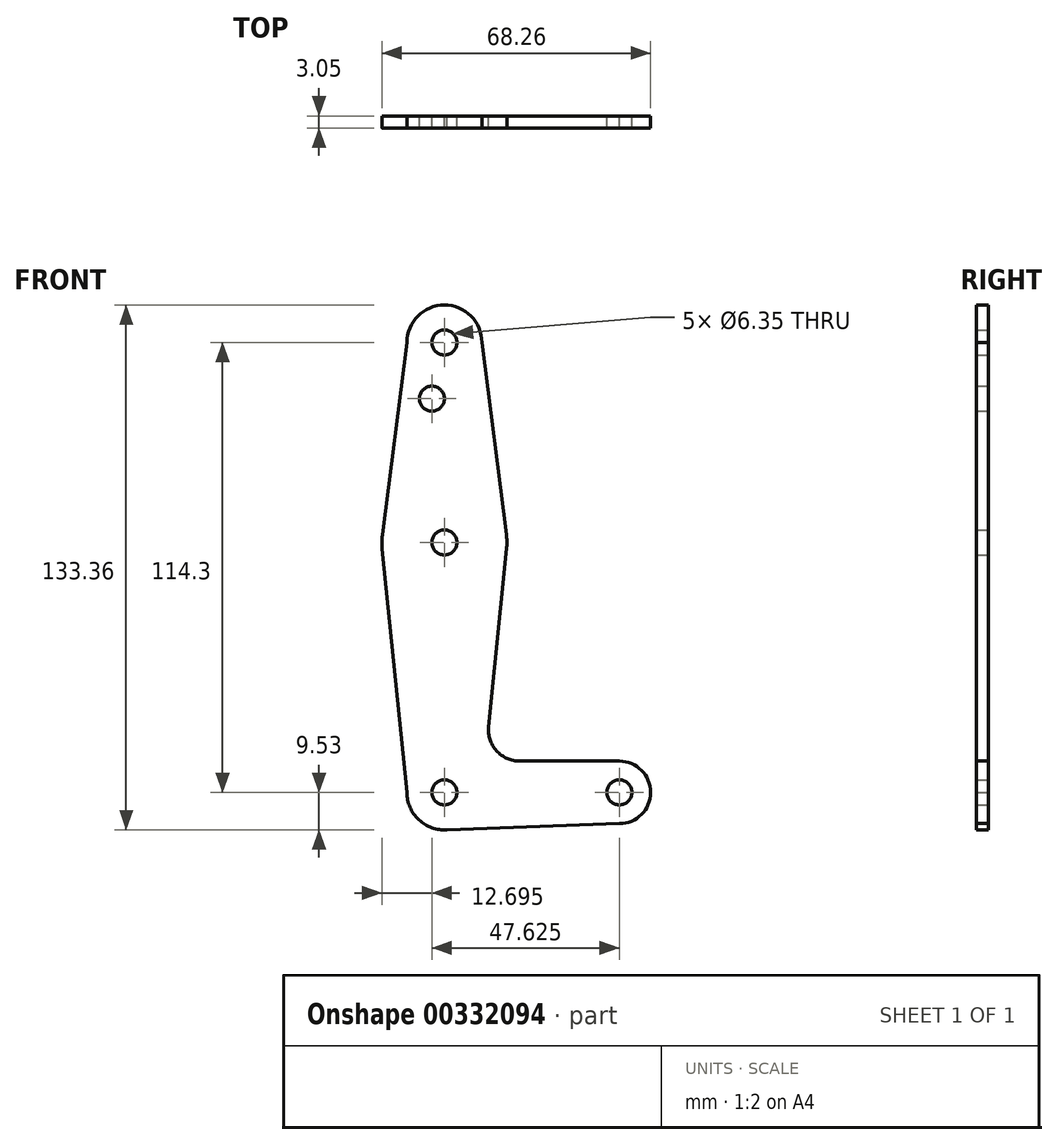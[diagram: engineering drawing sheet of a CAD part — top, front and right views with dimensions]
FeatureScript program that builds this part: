
annotation { "Feature Type Name" : "Feature", "Feature Type Description" : "" }
export const myFeature = defineFeature(function(context is Context, id is Id, definition is map)
    precondition{}
    {
        {
            var Q0;
            Q0=qCreatedBy(makeId("Front.planeOp"),FACE);
            var sketch = newSketch(context, id + "F0", { "sketchPlane" : qUnion([Q0])});
            skLineSegment(sketch, "E0", {"start": v(0, 0) * mm, "end": v(0, 114.3) * mm, "construction": true});
            skLineSegment(sketch, "E1", {"start": v(0, 0) * mm, "end": v(44.45, 0) * mm, "construction": true});
            skCircle(sketch, "E2", {"center": v(0, 0) * mm, "radius": 9.53 * mm});
            skCircle(sketch, "E3", {"center": v(0, 114.3) * mm, "radius": 9.53 * mm});
            skCircle(sketch, "E4", {"center": v(0, 63.5) * mm, "radius": 15.88 * mm});
            skCircle(sketch, "E5", {"center": v(44.45, 0) * mm, "radius": 7.94 * mm});
            skLineSegment(sketch, "E6", {"start": v(-9.53, 114.3) * mm, "end": v(-15.75, 65.5) * mm});
            skLineSegment(sketch, "E7", {"start": v(9.53, 114.3) * mm, "end": v(15.75, 65.5) * mm});
            skLineSegment(sketch, "E8", {"start": v(0, -9.52) * mm, "end": v(44.45, -7.94) * mm});
            skCircle(sketch, "E9", {"center": v(0, 114.3) * mm, "radius": 3.18 * mm});
            skCircle(sketch, "E10", {"center": v(0, 63.5) * mm, "radius": 3.18 * mm});
            skCircle(sketch, "E11", {"center": v(0, 0) * mm, "radius": 3.18 * mm});
            skCircle(sketch, "E12", {"center": v(44.45, 0) * mm, "radius": 3.18 * mm});
            skCircle(sketch, "E13", {"center": v(-3.18, 100.03) * mm, "radius": 3.18 * mm});
            skLineSegment(sketch, "E14", {"start": v(15.8, 61.91) * mm, "end": v(11.25, 16.68) * mm});
            skLineSegment(sketch, "E15", {"start": v(19.16, 7.94) * mm, "end": v(44.45, 7.94) * mm});
            skArc(sketch, "E16.filletArc", {"start": v(11.25, 16.68) * mm, "mid": v(13.26, 10.55) * mm, "end": v(19.16, 7.94) * mm});
            skLineSegment(sketch, "E17", {"start": v(-15.8, 61.9) * mm, "end": v(-9.52, 0) * mm});
            skSolve(sketch);
        }
        {
            var Q0;
            Q0 = qSketchRegion(id + "F0", true);
            extrude(context, id + "F1", {"entities" : qUnion([Q0]), "depth" : 3.05 * mm});
        }
    });
